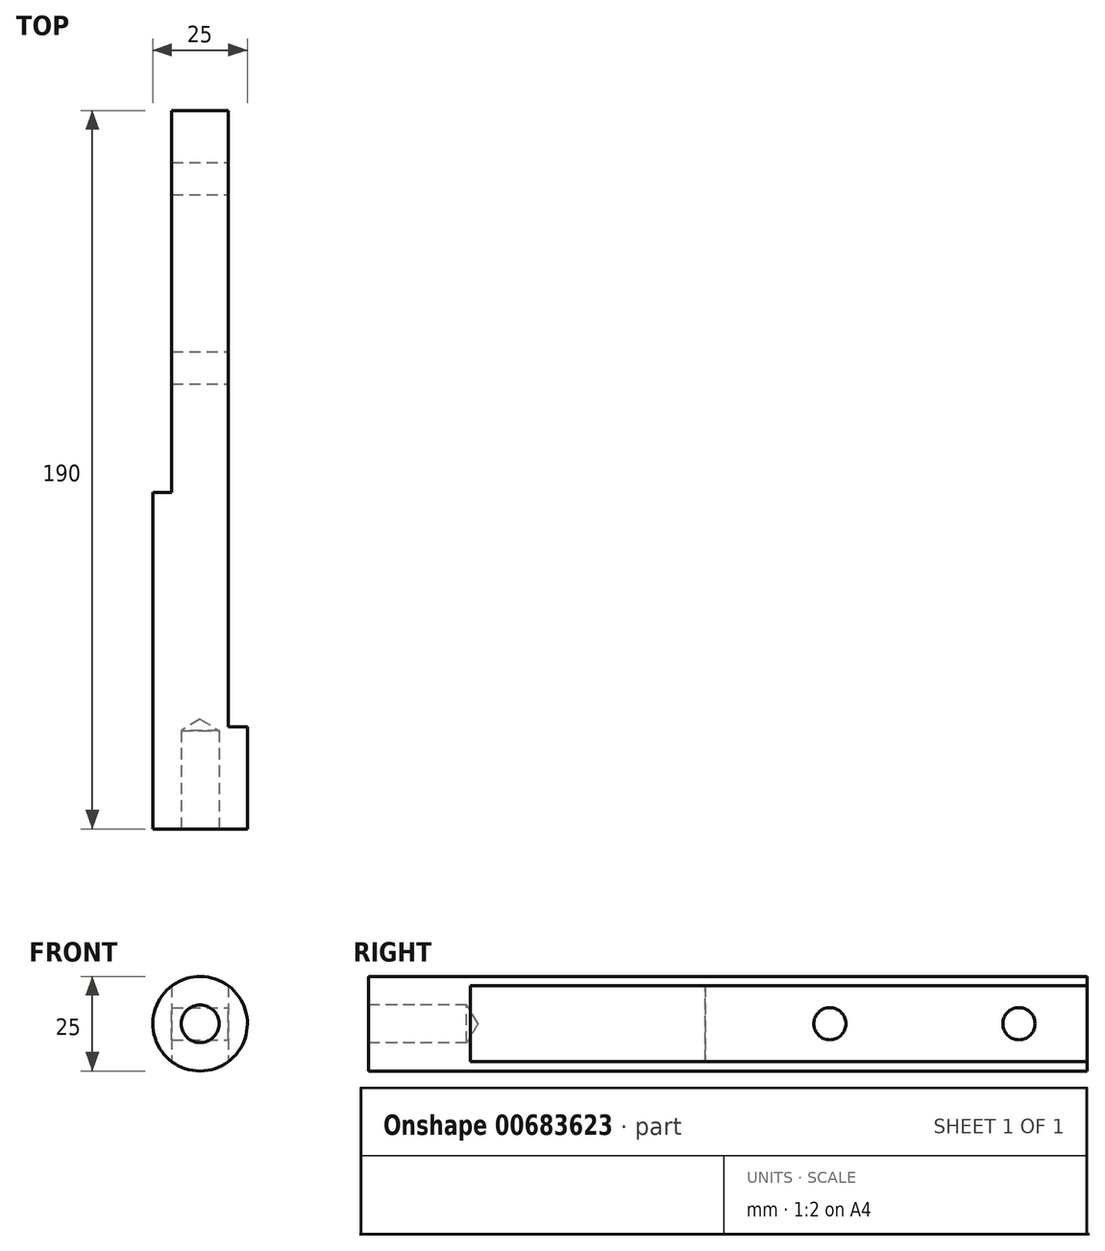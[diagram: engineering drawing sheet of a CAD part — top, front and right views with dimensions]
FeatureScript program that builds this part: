
annotation { "Feature Type Name" : "Feature", "Feature Type Description" : "" }
export const myFeature = defineFeature(function(context is Context, id is Id, definition is map)
    precondition{}
    {
        {
            var Q0;
            Q0=qCreatedBy(makeId("Front.planeOp"),FACE);
            var sketch = newSketch(context, id + "F0", { "sketchPlane" : qUnion([Q0])});
            skCircle(sketch, "E0", {"center": v(0, 0) * mm, "radius": 12.5 * mm});
            skSolve(sketch);
        }
        {
            var Q0;
            Q0 = qSketchRegion(id + "F0", true);
            extrude(context, id + "F1", {"entities" : qUnion([Q0]), "depth" : 190 * mm, "offsetDistance" : 25 * mm});
        }
        {
            var Q0;
            Q0=makeQuery(id+"F1.opExtrude","CAP_FACE",FACE,{"disambiguationData":[OSD([sQuery(id+"F0.wireOp",EDGE,"E0")])],"isStart":false});
            var sketch = newSketch(context, id + "F2", { "sketchPlane" : qUnion([Q0])});
            skCircle(sketch, "E1", {"center": v(0, 0) * mm, "radius": 5 * mm});
            skSolve(sketch);
        }
        {
            var Q0;
            Q0=sQuery(id+"F2.wireOp",VERTEX,"E1.center");
            var Q1;
            Q1=makeQuery(id+"F1.opExtrude","SWEPT_BODY",BODY,{"disambiguationData":[OSD([sQuery(id+"F0.wireOp",EDGE,"E0")])]});
            hole(context, id + "F3", {"style" : HoleStyle.SIMPLE, "endStyle" : HoleEndStyle.BLIND, "holeDiameter" : 10 * mm, "majorDiameter" : 5 * mm, "holeDepth" : 26 * mm, "isTappedThrough" : true, "tappedDepth" : 12 * mm, "tapClearance" : 3, "startFromSketch" : true, "locations" : qUnion([Q0]), "scope" : qUnion([Q1])});
        }
        {
            var Q0;
            Q0=qCreatedBy(makeId("Right.planeOp"),FACE);
            var sketch = newSketch(context, id + "F4", { "sketchPlane" : qUnion([Q0])});
            skCircle(sketch, "E2", {"center": v(-18, 0) * mm, "radius": 4.25 * mm});
            skCircle(sketch, "E3", {"center": v(-68, 0) * mm, "radius": 4.25 * mm});
            skSolve(sketch);
        }
        {
            var Q0;
            Q0 = qSketchRegion(id + "F4", true);
            extrude(context, id + "F5", {"entities" : qUnion([Q0]), "operationType" : NewBodyOperationType.REMOVE, "oppositeDirection" : true, "depth" : 25 * mm, "offsetDistance" : 25 * mm, "hasSecondDirection" : true, "secondDirectionOppositeDirection" : false, "secondDirectionDepth" : 25 * mm});
        }
        {
            var Q0;
            Q0=qCreatedBy(makeId("Right.planeOp"),FACE);
            cPlane(context, id + "F6", {"entities" : qUnion([Q0]), "cplaneType" : CPlaneType.OFFSET, "offset" : 12.5 * mm, "oppositeDirection" : true, "width" : 150 * mm, "height" : 150 * mm});
        }
        {
            var Q0;
            Q0=qCreatedBy(id+"F6.planeOp",FACE);
            var sketch = newSketch(context, id + "F7", { "sketchPlane" : qUnion([Q0])});
            skLineSegment(sketch, "E4.bottom", {"start": v(0, 12.5) * mm, "end": v(-101, 12.5) * mm});
            skLineSegment(sketch, "E4.top", {"start": v(0, -12.5) * mm, "end": v(-101, -12.5) * mm});
            skLineSegment(sketch, "E4.left", {"start": v(0, 12.5) * mm, "end": v(0, -12.5) * mm});
            skLineSegment(sketch, "E4.right", {"start": v(-101, 12.5) * mm, "end": v(-101, -12.5) * mm});
            skSolve(sketch);
        }
        {
            var Q0;
            Q0 = qSketchRegion(id + "F7", true);
            extrude(context, id + "F8", {"entities" : qUnion([Q0]), "operationType" : NewBodyOperationType.REMOVE, "depth" : 5 * mm, "offsetDistance" : 25 * mm});
        }
        {
            var Q0;
            Q0=qCreatedBy(makeId("Right.planeOp"),FACE);
            cPlane(context, id + "F9", {"entities" : qUnion([Q0]), "cplaneType" : CPlaneType.OFFSET, "offset" : 12.5 * mm, "width" : 150 * mm, "height" : 150 * mm});
        }
        {
            var Q0;
            Q0=qCreatedBy(id+"F9.planeOp",FACE);
            var sketch = newSketch(context, id + "F10", { "sketchPlane" : qUnion([Q0])});
            skLineSegment(sketch, "E5.bottom", {"start": v(0, 12.5) * mm, "end": v(-163, 12.5) * mm});
            skLineSegment(sketch, "E5.top", {"start": v(0, -12.5) * mm, "end": v(-163, -12.5) * mm});
            skLineSegment(sketch, "E5.left", {"start": v(0, 12.5) * mm, "end": v(0, -12.5) * mm});
            skLineSegment(sketch, "E5.right", {"start": v(-163, 12.5) * mm, "end": v(-163, -12.5) * mm});
            skSolve(sketch);
        }
        {
            var Q0;
            Q0 = qSketchRegion(id + "F10", true);
            extrude(context, id + "F11", {"entities" : qUnion([Q0]), "operationType" : NewBodyOperationType.REMOVE, "oppositeDirection" : true, "depth" : 5 * mm, "offsetDistance" : 25 * mm});
        }
    });
